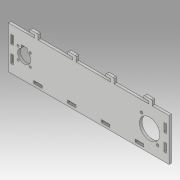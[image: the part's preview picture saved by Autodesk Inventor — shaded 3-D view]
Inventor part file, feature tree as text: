
AUTODESK INVENTOR PART (.ipt)
format: ipt  version: 2019.3 (Build 233278000, 278)  size: 220,672 bytes
history: native  units: mm
features: extrude x1, sketch x1
ambient origin geometry x8: Origin, YZ Plane, XZ Plane, XY Plane, X Axis, Y Axis, Z Axis, Center Point
bodies: Body1 (feature_tree)
feature tree (2):
  extrude  "Extrusion4"  Depth=50.0mm
  sketch  "Sketch1"  dims[d6=190.0mm d7=50.0mm d19=20.0mm d23=10.0mm d24=3.0mm d25=3.0mm d26=4.0mm d27=1.0mm d28=45.0mm d29=45.0mm d30=45.0mm d31=31.0mm d32=10.0mm d33=3.0mm d34=3.0mm d35=10.0mm d36=10.0mm d37=3.0mm d38=24.0mm d39=5.0mm d40=15.5mm d41=10.25mm d42=7.0mm d43=2.5mm d44=14.5mm d45=14.5mm d46=7.25mm d47=7.25mm d48=5.0mm d51=10.0mm d52=30.0mm d53=30.0mm d54=30.0mm d55=30.0mm d56=3.0mm d57=3.0mm d60=3.0mm d61=31.0mm d62=26.0mm d63=2.0mm d64=2.0mm d65=2.0mm d66=2.0mm d69=3.0mm d70=0.0mm]
